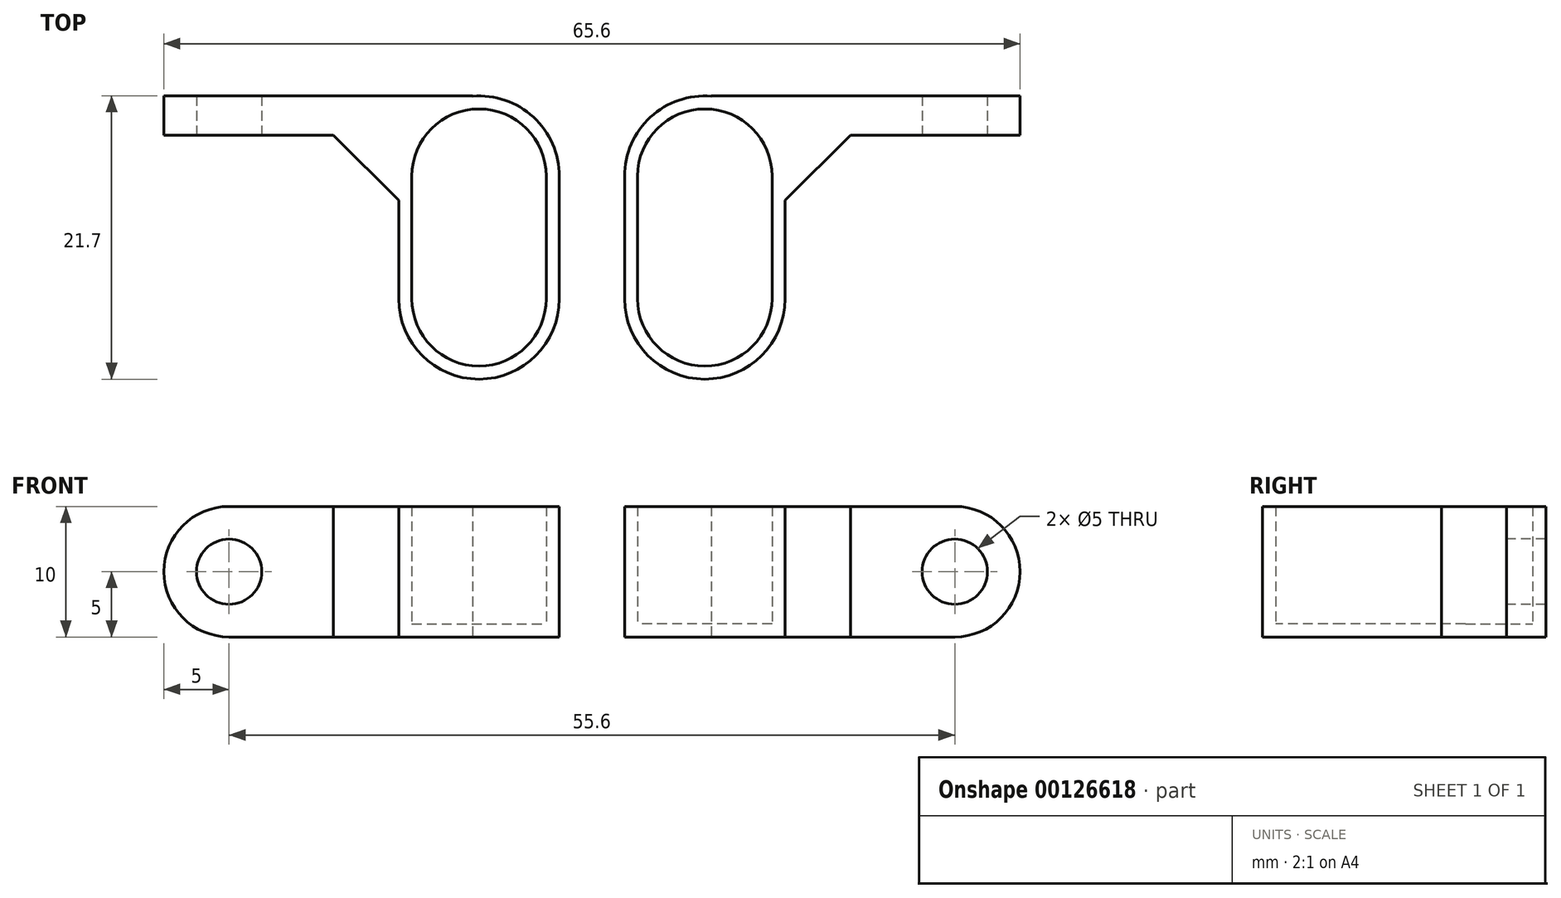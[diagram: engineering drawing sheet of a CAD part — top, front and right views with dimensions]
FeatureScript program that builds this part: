
annotation { "Feature Type Name" : "Feature", "Feature Type Description" : "" }
export const myFeature = defineFeature(function(context is Context, id is Id, definition is map)
    precondition{}
    {
        {
            var Q0;
            Q0=qCreatedBy(makeId("Top.planeOp"),FACE);
            var sketch = newSketch(context, id + "F0", { "sketchPlane" : qUnion([Q0])});
            skLineSegment(sketch, "E0.bottom", {"start": v(5.15, 0) * mm, "end": v(5.15, 0) * mm});
            skLineSegment(sketch, "E0.top", {"start": v(5.15, -19.7) * mm, "end": v(5.15, -19.7) * mm});
            skLineSegment(sketch, "E0.left", {"start": v(0, -5.15) * mm, "end": v(0, -14.55) * mm});
            skLineSegment(sketch, "E0.right", {"start": v(10.3, -5.15) * mm, "end": v(10.3, -14.55) * mm});
            skPoint(sketch, "E1.visualSharp", {"position": v(0, 0) * mm});
            skArc(sketch, "E1.filletArc", {"start": v(5.15, 0) * mm, "mid": v(1.5, -1.5) * mm, "end": v(0, -5.15) * mm});
            skPoint(sketch, "E2.visualSharp", {"position": v(10.3, -19.7) * mm});
            skArc(sketch, "E2.filletArc", {"start": v(5.15, -19.7) * mm, "mid": v(8.8, -18.2) * mm, "end": v(10.3, -14.55) * mm});
            skPoint(sketch, "E3.visualSharp", {"position": v(10.3, 0) * mm});
            skArc(sketch, "E3.filletArc", {"start": v(10.3, -5.15) * mm, "mid": v(8.8, -1.5) * mm, "end": v(5.15, 0) * mm});
            skPoint(sketch, "E4.visualSharp", {"position": v(0, -19.7) * mm});
            skArc(sketch, "E4.filletArc", {"start": v(0, -14.55) * mm, "mid": v(1.5, -18.2) * mm, "end": v(5.15, -19.7) * mm});
            skArc(sketch, "E5.0", {"start": v(11.3, -5.15) * mm, "mid": v(9.5, -0.8) * mm, "end": v(5.15, 1) * mm});
            skLineSegment(sketch, "E5.1", {"start": v(-1, -5.15) * mm, "end": v(-1, -14.55) * mm});
            skArc(sketch, "E5.2", {"start": v(-1, -14.55) * mm, "mid": v(0.8, -18.9) * mm, "end": v(5.15, -20.7) * mm});
            skArc(sketch, "E5.3", {"start": v(5.15, 1) * mm, "mid": v(0.8, -0.8) * mm, "end": v(-1, -5.15) * mm});
            skArc(sketch, "E5.4", {"start": v(5.15, -20.7) * mm, "mid": v(9.5, -18.9) * mm, "end": v(11.3, -14.55) * mm});
            skLineSegment(sketch, "E5.5", {"start": v(11.3, -5.15) * mm, "end": v(11.3, -14.55) * mm});
            skSolve(sketch);
        }
        {
            var Q0;
            Q0=makeQuery(id+"F0.imprint","IMPRINT",FACE,{"disambiguationData":[TD([[makeQuery(id+"F0.imprint","IMPRINT",EDGE,{"derivedFrom":sQuery(id+"F0.wireOp",EDGE,"E0.left")}),1.0]])]});
            extrude(context, id + "F1", {"entities" : qUnion([Q0]), "depth" : 1 * mm});
        }
        {
            var Q0;
            Q0=qSketchRegion(id+"F0",true);
            extrude(context, id + "F2", {"entities" : qUnion([Q0]), "operationType" : NewBodyOperationType.ADD, "depth" : 10 * mm});
        }
        {
            var Q0;
            Q0=makeQuery(id+"F2.opExtrude","SWEPT_FACE",FACE,{"disambiguationData":[OSD([sQuery(id+"F0.wireOp",EDGE,"E5.5")])]});
            var sketch = newSketch(context, id + "F3", { "sketchPlane" : qUnion([Q0])});
            skLineSegment(sketch, "E6", {"start": v(1, 10) * mm, "end": v(1, 0) * mm});
            skLineSegment(sketch, "E7", {"start": v(-20.7, 0) * mm, "end": v(-20.7, 10) * mm});
            skLineSegment(sketch, "E8.bottom", {"start": v(1, 10) * mm, "end": v(-2, 10) * mm});
            skLineSegment(sketch, "E8.top", {"start": v(1, 0) * mm, "end": v(-2, 0) * mm});
            skLineSegment(sketch, "E8.right", {"start": v(-2, 10) * mm, "end": v(-2, 0) * mm});
            skSolve(sketch);
        }
        {
            var Q0;
            Q0=qSketchRegion(id+"F3",true);
            extrude(context, id + "F4", {"entities" : qUnion([Q0]), "operationType" : NewBodyOperationType.ADD, "oppositeDirection" : true, "depth" : 5.65 * mm, "hasSecondDirection" : true, "secondDirectionOppositeDirection" : false, "secondDirectionDepth" : 18 * mm});
        }
        {
            var Q0;
            Q0=makeQuery(id+"F4.boolean.opBoolean","MERGE",FACE,{"derivedFrom":[makeQuery(id+"F2.opExtrude","CAP_FACE",FACE,{"disambiguationData":[OSD([sQuery(id+"F0.wireOp",EDGE,"E0.left"),sQuery(id+"F0.wireOp",EDGE,"E0.right"),sQuery(id+"F0.wireOp",EDGE,"E1.filletArc"),sQuery(id+"F0.wireOp",EDGE,"E2.filletArc"),sQuery(id+"F0.wireOp",EDGE,"E3.filletArc"),sQuery(id+"F0.wireOp",EDGE,"E4.filletArc"),sQuery(id+"F0.wireOp",EDGE,"E5.0"),sQuery(id+"F0.wireOp",EDGE,"E5.1"),sQuery(id+"F0.wireOp",EDGE,"E5.2"),sQuery(id+"F0.wireOp",EDGE,"E5.3"),sQuery(id+"F0.wireOp",EDGE,"E5.4"),sQuery(id+"F0.wireOp",EDGE,"E5.5")])],"isStart":false}),makeQuery(id+"F4.opExtrude","SWEPT_FACE",FACE,{"disambiguationData":[OSD([sQuery(id+"F3.wireOp",EDGE,"E8.bottom")])]})]});
            var sketch = newSketch(context, id + "F5", { "sketchPlane" : qUnion([Q0])});
            skArc(sketch, "E9", {"start": v(10.3, -5.15) * mm, "mid": v(5.15, 0) * mm, "end": v(0, -5.15) * mm});
            skLineSegment(sketch, "E10", {"start": v(0, -5.15) * mm, "end": v(10.3, -5.15) * mm});
            skSolve(sketch);
        }
        {
            var Q0;
            {var subQ12=sQuery(id+"F5.wireOp",EDGE,"E10");Q0=makeQuery(id+"F5.imprint","IMPRINT",FACE,{"disambiguationData":[TD([[makeQuery(id+"F5.imprint","IMPRINT",EDGE,{"derivedFrom":subQ12}),1.0]])]});}
            var Q1;
            {var subQ1=sQuery(id+"F3.wireOp",EDGE,"E8.right");var subQ2=sQuery(id+"F3.wireOp",EDGE,"E8.bottom");var subQ9=makeQuery(id+"F4.opExtrude","SWEPT_FACE",FACE,{"disambiguationData":[OSD([subQ1])]});var subQ10=makeQuery(id+"F4.boolean.opBoolean","SPLIT",EDGE,{"disambiguationData":[TD([subQ9])],"derivedFrom":makeQuery(id+"F4.opExtrude","CAP_EDGE",EDGE,{"disambiguationData":[OSD([subQ2])],"isStart":false})});Q1=makeQuery(id+"F5.imprint","IMPRINT",FACE,{"disambiguationData":[TD([[makeQuery(id+"F5.imprint","IMPRINT",EDGE,{"derivedFrom":subQ10}),1.0]])]});}
            extrude(context, id + "F6", {"entities" : qUnion([Q0, Q1]), "operationType" : NewBodyOperationType.REMOVE, "oppositeDirection" : true, "depth" : 9 * mm});
        }
        {
            var Q0;
            Q0=makeQuery(id+"F4.boolean.opBoolean","INTERSECT",EDGE,{"derivedFrom":[makeQuery(id+"F2.opExtrude","SWEPT_FACE",FACE,{"disambiguationData":[OSD([sQuery(id+"F0.wireOp",EDGE,"E5.0"),sQuery(id+"F0.wireOp",EDGE,"E5.3")])]}),makeQuery(id+"F4.opExtrude","SWEPT_FACE",FACE,{"disambiguationData":[OSD([sQuery(id+"F3.wireOp",EDGE,"E8.right")])]})]});
            chamfer(context, id + "F7", {"entities" : qUnion([Q0]), "width" : 5 * mm, "tangentPropagation" : true});
        }
        {
            var Q0;
            Q0=makeQuery(id+"F4.opExtrude","CAP_EDGE",EDGE,{"disambiguationData":[OSD([sQuery(id+"F3.wireOp",EDGE,"E8.bottom")])],"isStart":true});
            var Q1;
            Q1=makeQuery(id+"F4.opExtrude","CAP_EDGE",EDGE,{"disambiguationData":[OSD([sQuery(id+"F3.wireOp",EDGE,"E8.top")])],"isStart":true});
            fillet(context, id + "F8", {"entities" : qUnion([Q0, Q1]), "radius" : 5 * mm, "tangentPropagation" : true, "allowEdgeOverflow" : false});
        }
        {
            var Q0;
            {var subQ13=sQuery(id+"F3.wireOp",EDGE,"E8.right");var subQ14=sQuery(id+"F3.wireOp",EDGE,"E8.top");Q0=makeQuery(id+"F4.boolean.opBoolean","SPLIT",FACE,{"disambiguationData":[TD([makeQuery(id+"F4.opExtrude","SWEPT_FACE",FACE,{"disambiguationData":[OSD([subQ14])]})])],"derivedFrom":makeQuery(id+"F4.opExtrude","SWEPT_FACE",FACE,{"disambiguationData":[OSD([subQ13])]})});}
            var sketch = newSketch(context, id + "F9", { "sketchPlane" : qUnion([Q0])});
            skCircle(sketch, "E11", {"center": v(24.3, 5) * mm, "radius": 2.5 * mm});
            skPoint(sketch, "E12.orphan", {"position": v(24.3, 10) * mm});
            skPoint(sketch, "E13.orphan", {"position": v(29.3, 5) * mm});
            skPoint(sketch, "E14.start.orphan", {"position": v(24.3, 0) * mm});
            skSolve(sketch);
        }
        {
            var Q0;
            Q0=qSketchRegion(id+"F9",true);
            var Q1;
            Q1=makeQuery(id+"F9.imprint","IMPRINT",FACE,{"disambiguationData":[TD([[makeQuery(id+"F9.imprint","IMPRINT",EDGE,{"derivedFrom":sQuery(id+"F9.wireOp",EDGE,"E11")}),1.0]])]});
            extrude(context, id + "F10", {"entities" : qUnion([Q0, Q1]), "operationType" : NewBodyOperationType.REMOVE, "oppositeDirection" : true, "depth" : 25 * mm});
        }
        {
            var Q0;
            Q0=makeQuery(id+"F1.opExtrude","SWEPT_BODY",BODY,{"disambiguationData":[OSD([sQuery(id+"F0.wireOp",EDGE,"E0.left"),sQuery(id+"F0.wireOp",EDGE,"E0.right"),sQuery(id+"F0.wireOp",EDGE,"E1.filletArc"),sQuery(id+"F0.wireOp",EDGE,"E2.filletArc"),sQuery(id+"F0.wireOp",EDGE,"E3.filletArc"),sQuery(id+"F0.wireOp",EDGE,"E4.filletArc")])]});
            var Q1;
            Q1=makeQuery(id+"F2.opExtrude","SWEPT_FACE",FACE,{"disambiguationData":[OSD([sQuery(id+"F0.wireOp",EDGE,"E5.1")])]});
            mirror(context, id + "F11", {"entities" : qUnion([Q0]), "mirrorPlane" : qUnion([Q1])});
        }
        {
            var Q0;
            Q0=makeQuery(id+"F11.opPattern","COPY",BODY,{"derivedFrom":makeQuery(id+"F1.opExtrude","SWEPT_BODY",BODY,{"disambiguationData":[OSD([sQuery(id+"F0.wireOp",EDGE,"E0.left"),sQuery(id+"F0.wireOp",EDGE,"E0.right"),sQuery(id+"F0.wireOp",EDGE,"E1.filletArc"),sQuery(id+"F0.wireOp",EDGE,"E2.filletArc"),sQuery(id+"F0.wireOp",EDGE,"E3.filletArc"),sQuery(id+"F0.wireOp",EDGE,"E4.filletArc")])]}),"instanceName":"1"});
            var Q1;
            Q1=makeQuery(id+"F4.opExtrude","SWEPT_EDGE",EDGE,{"disambiguationData":[OSD([sQuery(id+"F3.wireOp",EDGE,"E8.bottom"),sQuery(id+"F3.wireOp",EDGE,"E6")])]});
            transform(context, id + "F12", {"entities" : qUnion([Q0]), "transformType" : TransformType.TRANSLATION_DISTANCE, "transformDirection" : qUnion([Q1]), "distance" : 5 * mm, "oppositeDirection" : true, "makeCopy" : false});
        }
    });
